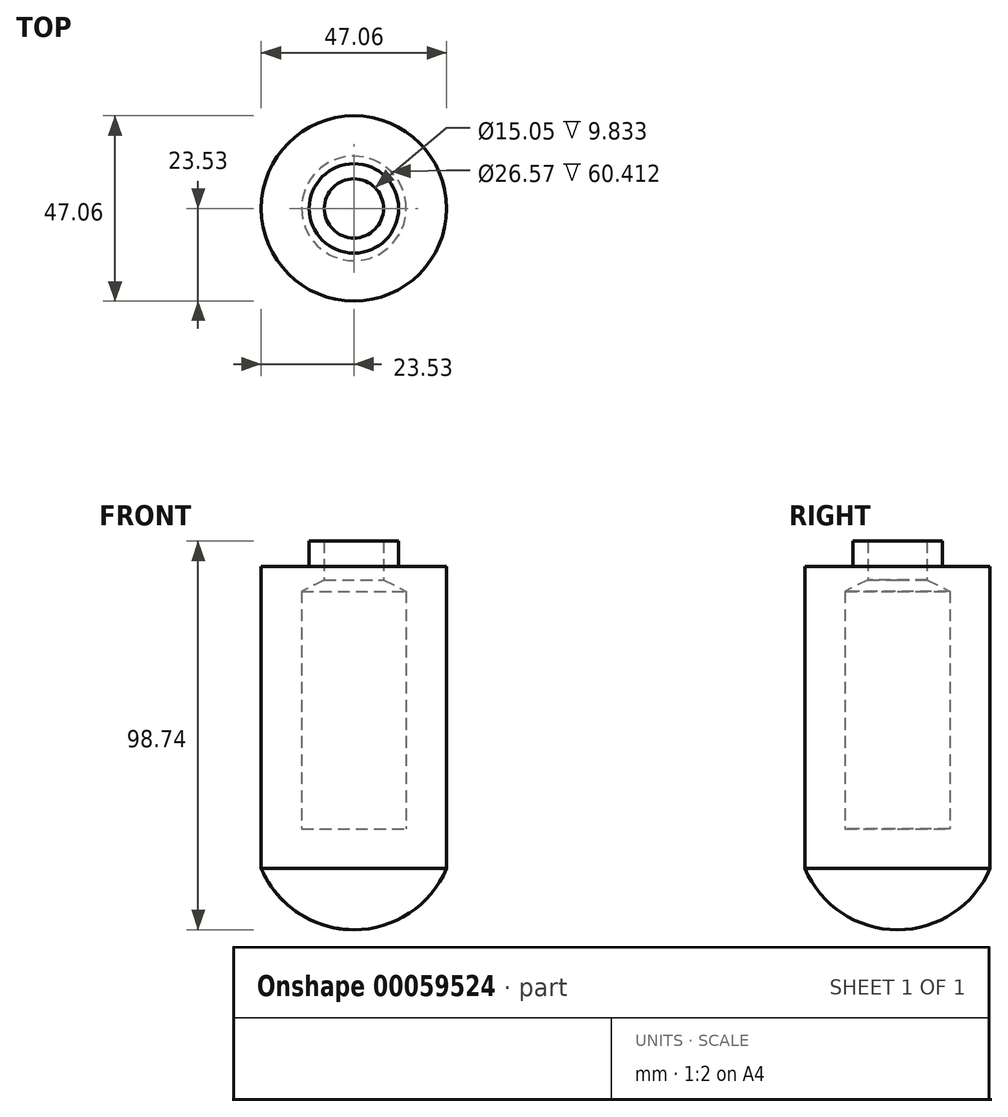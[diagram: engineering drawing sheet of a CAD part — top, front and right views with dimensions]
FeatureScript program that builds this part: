
annotation { "Feature Type Name" : "Feature", "Feature Type Description" : "" }
export const myFeature = defineFeature(function(context is Context, id is Id, definition is map)
    precondition{}
    {
        {
            var Q0;
            Q0=qCreatedBy(makeId("Front.planeOp"),FACE);
            var sketch = newSketch(context, id + "F0", { "sketchPlane" : qUnion([Q0])});
            skLineSegment(sketch, "E0", {"start": v(0, 0) * mm, "end": v(13.29, 0) * mm});
            skLineSegment(sketch, "E1", {"start": v(13.29, 0) * mm, "end": v(13.29, 60.41) * mm});
            skLineSegment(sketch, "E2", {"start": v(13.29, 60.41) * mm, "end": v(7.52, 63.32) * mm});
            skLineSegment(sketch, "E3", {"start": v(7.52, 63.32) * mm, "end": v(7.52, 73.16) * mm});
            skLineSegment(sketch, "E4", {"start": v(7.52, 73.16) * mm, "end": v(11.37, 73.16) * mm});
            skLineSegment(sketch, "E5", {"start": v(11.37, 73.16) * mm, "end": v(11.37, 66.67) * mm});
            skLineSegment(sketch, "E6", {"start": v(11.37, 66.67) * mm, "end": v(23.53, 66.67) * mm});
            skLineSegment(sketch, "E7", {"start": v(23.53, 66.67) * mm, "end": v(23.53, -10.04) * mm});
            skLineSegment(sketch, "E8", {"start": v(0, -25.58) * mm, "end": v(0, 0) * mm});
            skArc(sketch, "E9", {"start": v(0, -25.58) * mm, "mid": v(14.1, -21.35) * mm, "end": v(23.53, -10.04) * mm});
            skPoint(sketch, "E10.orphan", {"position": v(0, -10.04) * mm});
            skSolve(sketch);
        }
        {
            var Q0;
            Q0=makeQuery(id+"F0.imprint","IMPRINT",FACE,{"disambiguationData":[TD([[makeQuery(id+"F0.imprint","IMPRINT",EDGE,{"derivedFrom":sQuery(id+"F0.wireOp",EDGE,"E0")}),-1.0]])]});
            var Q1;
            Q1=sQuery(id+"F0.wireOp",EDGE,"E8");
            revolve(context, id + "F1", {"entities" : qUnion([Q0]), "axis" : qUnion([Q1]), "revolveType" : RevolveType.FULL});
        }
    });
